# Revit family: Sanitary_Shower-screens_Duscholux_DuschoGravity_Slider-twin-doors-shower
name_source: partatom
category: Plumbing Fixtures
revit_build: Autodesk Revit 2016 (Build: 20150220_1215(x64)
units: mm (PartAtom-declared; Revit-internal decimal feet)

## family parameters
Always vertical = Yes
Cut with Voids When Loaded = No
OmniClass Number = 23.45.00.00
OmniClass Title = Sanitary, Laundry, and Cleaning Equipment
Part Type = Normal
Room Calculation Point = No
Round Connector Dimension = Use Diameter
Shared = No
Work Plane-Based = No

## types (3) — shared parameters
Anti-Lime Treatment = FeelNet 3D Included
Assembly Code = C1030200
Brand = Duscholux
Certified Quality UNE EN 14428 = http://www.duscholux.es
Combinations = Lateral 90°
Components = Eropean components
Configuration enclosure = http://configuratumampara.duscholux.es
Description = 2 fixed segments + slider twin doors
Design country = Germany
Edition number = 1
Environmental Management ISO 14001 = ECOEMBES Certificate
Fact sheet = http://blob.duscholux.es
Glass Material = Glass_Material-Duscholux
Glass in Building UNE EN 12150 = CE Conformity marking
IFC Classification = Furnishing Element
Image = http://www.duscholux.es
Maintenance and Cleaning = http://www.duscholux.es
Manufacturer = Duscholux Ibérica, S.A.
Manufacturer country = Spain / Germany
Manufacturer name = Duscholux Ibérica, S.A.
Min Max Width = 1400 mm  [stored 4.59318 ft]
NBS Reference Code = 45-35-70
NBS Reference Description = Shower Enclosures
Net Weight (Kg) = 63
Opening System = Sliding
Opening System Image = http://blob.duscholux.es
Optional = Towel rail / Shelf
Product family = Duscho Gravity
Product group = Front for shower
Products = http://www.duscholux.es
Ref. = KAB
Series = DuschoGravity
Sliding Door Width = 356 mm
Technical Inspection Certificate (Applus) = http://www.duscholux.es
Thickness Safety Glass Fixed Panel = 8 mm  [stored 0.0262467 ft]
Thickness Safety Glass Sliding = 5 mm  [stored 0.0164042 ft]
UNSPSC Code = 30181507
URL = http://www.duscholux.es
Uniclass 2015 Code = PR-40-20-06-79
Uniclass 2015 Description = Shower Enclosures
Width = 1400 mm  [stored 4.59318 ft]
zero-valued in all types: Opening Door, Opening Percentage

## per-type parameters (varying)
| type | Accesories Material | Frame Material | Handle Height | Handle Material | Height | Max Height |
| Platinum Aluminium Finish | Chrome_Finish | Platinum Aluminium Finish | 1000 mm  [stored 3.28084 ft] | Chrome_Finish | 2000 mm  [stored 6.56168 ft] | 2000 mm  [stored 6.56168 ft] |
| White Aluminium Finish | White Aluminium Finish | White Finish | 1000 mm  [stored 3.28084 ft] | White Finish | 2000 mm  [stored 6.56168 ft] | 2000 mm  [stored 6.56168 ft] |
| Silver Matt Aluminium Finish | Chrome_Finish | Silver Matt Aluminium Finish | 800 mm | Chrome_Finish | 1600 mm | 1600 mm |

note: [stored X ft] marks values corroborated as IEEE doubles in the binary element streams (Revit-internal decimal feet)
